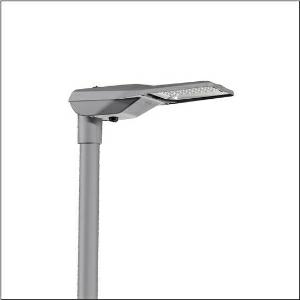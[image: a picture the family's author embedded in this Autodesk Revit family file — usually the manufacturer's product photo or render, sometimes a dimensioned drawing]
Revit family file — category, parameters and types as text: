
# Revit family: streetlight_sl_21_iq_mini___st1_0a_5xe2d61y08hb_d678
name_source: partatom
category: Lighting Fixtures
units: mm (PartAtom-declared; Revit-internal decimal feet)

## family parameters
Cut with Voids When Loaded = No
Host = Face
Light Source = No
Part Type = Normal
Room Calculation Point = No
Round Connector Dimension = Use Diameter
Shared = No

## types (1)
- --- (1 x LED, 8460 lm, 71 W, 2700K)
    Apparent Load = 71 VA
    CIE Flux Codes = 37 72 97 100 100
    Color Rendering = 70
    Color Temperature = 2700K
    Default Elevation = 1800 mm
    Description = Streetlight SL 21 iQ mini, mast luminaire, primary light control with lens, of PMMA, primary optical cover: cover, of toughened safety glass, transparent, light distribution: ST1.0a, light emission: direct distribution, primary light characteristic: asymmetric, installation type: post-top, side-entry, LED, High Power LED, rated luminous flux: 8.460lm, luminous efficacy: 119lm/W, light colour: 727, colour temperature: 2700K, control gear: iQ-Street Remote, D4i with power reduction, control: pre-setting: logarithmic dimming characteristic, Street-Remote, Auto-Match, Temp-Guard, Lumen-Switch, Night-Set, Smart-Wire, Light-Fading, Desk-Remote (wireless, voltage-free reading and setting of iQ features in the workshop via application-optimized NFC function/RFID function), optimised constant luminous flux control (CLO 2.0), mains connection: 220..240V, AC, 50/60Hz, start of lifetime: 71W, end of service life: 75W, reduction: 30W, luminaire housing, of diecast aluminium, powder-coated, SITECO metallic grey (DB 702S), corrosivity category C5 high according to DIN EN ISO 12944, please order mast flange separately, inclination adjustable: 0°, 5°, 10°, 15°, sealing non-destructively replaceable, multi-level sealing system, length: 628mm, width: 235mm, height: 110mm, mast flange for spigot size: 42mm (side-entry): 5XC10008XM4, 60/48mm (side-entry/post-top): 5XC10108XM2, 76/60mm (side-entry/post-top): 5XC10108XM1, mounting height: 4..8m, Smart Interface below and above, protection rating (complete): IP66, insulation class (complete): insulation class II (safety insulation), certification: CE, ENEC, ENEC+, VDE, impact resistance: IK10, permissible operating ambient temperature for outdoor applications: -40..+50°C, standard-compliant lighting for roads and squares, packaging unit: 1 piece

Light Distribution: ST1.0a
    Height = 110 mm
    Lamp = 1 x LED
    Lamp Light Flux = 8460 lm
    Lamp Power = 71 W
    Lamp count = 1
    Length = 625 mm
    Luminous efficacy = 119 lm/W
    Manufacturer = Siteco
    ModVariant = No
    Model = 5XE2D61Y08HB
    Number of Poles = 1
    OnlyDefault = Yes
    Power Factor = 1
    Product Name = Streetlight SL 21 iQ mini | ST1.0a
    Product group = mast luminaire | pylon top
    ProductGroupID = 6100
    Protection Class = Protection class II
    Protection Degree = IP 66
    RLX_Detail_Level = 1
    RLX_Emergency_Light_Flux = 0 lm
    RLX_Emergency_Type = 0
    RLX_Emergency_Type_DB = No
    RlxData = <blob elided: 92205 chars, md5=6f1f112d>
    Socket = socket
    Standby Power = 0 W
    System Light Flux = 8460 lm
    System Power = 71 W
    Type Comments = factory setting: luminous flux: 100 % | dim-lin: 254 | 716 mA
    Type Image = l_1003514.jpg
    URL = http://relux.com
    VarID = @adj_115077
    Voltage = 0 V
    Weight = 0.00 kg
    Width = 234 mm

## geometry (parser evidence)
native form markers: Blend x4, Sweep x12
no freeform markers — native parametric forms only
